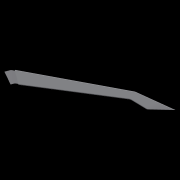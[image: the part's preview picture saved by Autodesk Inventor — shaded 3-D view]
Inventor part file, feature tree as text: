
AUTODESK INVENTOR PART (.ipt)
format: ipt  version: 2020 (Build 240168000, 168)  size: 9,528,320 bytes
history: native  units: in
note: dims shown in document units (in); Inventor stores cm internally (conversion verified against a paired STEP export)
features: other x166, extrude x71, fillet x44, projected_geometry x9, sketch x6, hole x4, loft x3, reference x2, plane x1, move_body x1
ambient origin geometry x8: Origin, YZ Plane, XZ Plane, XY Plane, X Axis, Y Axis, Z Axis, Center Point
bodies: Body (feature_tree), BodyFeature (feature_tree), BodyCut (feature_tree), BodyCutFeature (feature_tree), BodyCutFilletFeature (feature_tree), BodyCutCombineFeature (feature_tree), BodyCutEdgeFilletFeature (feature_tree), BodyRibFrontFilletsFeature (feature_tree), BodyBackRibFilletsFeature (feature_tree), BodyFretboardFilletsFeature (feature_tree), BodyFrontTopFilletsFeature (feature_tree), BodyFrontBottomFilletsFeature (feature_tree), BodyFrontNeckFilletsFeature (feature_tree), Solid22 (feature_tree), Solid23 (feature_tree), Solid62 (feature_tree), Solid64 (feature_tree), Solid65 (feature_tree), Solid68 (feature_tree), Solid50 (feature_tree), Solid52 (feature_tree), Solid54 (feature_tree), Solid56 (feature_tree), Solid57 (feature_tree), Solid59 (feature_tree)
feature tree (307):
  other  "MainBody"
  extrude  "NeckMountsProfileFeature"  Depth=0.5in TaperAngle=0.0deg
  other  "NeckPlane"
  extrude  "8StringFeature"  Depth=4.5in
  extrude  "6StringFeature"  Depth=1.12in
  extrude  "HornFeature"  Depth=0.6788in
  other  "6StringNeckFeature"
  other  "8StringNeckFeature"
  fillet  "InsideCornerFilletsFeature1/8"  Radius=0.6788in
  fillet  "OutsideFilletsFeature1/2"  Radius=0.125in
  fillet  "NeckMountOutsideFilletsFeature1/4"  Radius=0.5in
  fillet  "TipFilletsFeature1/8"  Radius=0.125in
  fillet  "BottomHornTipFilletFeature1/10"  Radius=0.1in
  fillet  "BottomHornFilletsFeature1/8"  Radius=0.125in
  fillet  "InsideHandleFilletsFeature1/2"  Radius=0.5in
  fillet  "InsideHandleFilletsFeature1/8"  Radius=0.125in
  fillet  "InsideTopHornFilletsFeature1/4"  Radius=0.25in
  fillet  "InsideTopHornFilletsFeature1/2"  Radius=0.5in
  fillet  "InsideBottomHornFilletsFeature1/4"  Radius=0.25in
  other  "PickupsOriginal"
  other  "MiddlePlane"
  other  "PickupsCustom"
  other  "PickupsModified"
  extrude  "TopPickupsIndentFeature"  Depth=0.0515in
  extrude  "BottomPickupsIndentFeature"  Depth=0.05in
  extrude  "TopPickupHolesFeature"  Depth=0.05in
  extrude  "BottomPickupHolesFeature"  Depth=0.05in
  fillet  "PickupIndentFilletsFeature"  Radius=5.7in
  other  "Frets"
  other  "FretsPreview"
  other  "TopHornHandleIndent"
  extrude  "TopHornBodyHandleFeature"  Depth=0.05in
  extrude  "TopHornHornHandleFeature"  Depth=0.05in
  other  "HornSculptFeature"
  other  "TopHornHandleFront"
  extrude  "TopHornHandleFrontFeature"  Depth=0.05in
  extrude  "TopHornHandleFront2Feature"  TaperAngle=45.0deg  [1 undecoded]
  extrude  "TopHornHandleFront3Feature"  TaperAngle=120.0deg  [1 undecoded]
  other  "TopHornHandleBack"
  extrude  "TopHornHandleBackFeature"  Depth=0.05in
  extrude  "TopHornHandleBack2Feature"  Depth=0.05in
  extrude  "TopHandleFeature"  Depth=0.05in
  extrude  "TopHandleFrontFeature"  Depth=0.05in
  extrude  "TopHandleBackFeature"  Depth=0.05in
  other  "Tuners"
  hole  "TunerHolesFeature"  [1 undecoded]
  other  "LogoMount"
  extrude  "LogoMountFeature"  Depth=0.05in
  other  "SideProfile"
  extrude  "SideProfileFeature"  Depth=0.05in
  other  "KeyboardCompartmentSidePlane"
  extrude  "KeyboardCompartmentFeature"  Depth=0.05in
  fillet  "KeyboardCompartmentFilletsFeature"  Radius=1.7in
  other  "ControlsBottom"
  other  "ControlsTop2"
  other  "ControlsTop1"
  extrude  "ControlsTop1Feature"  Depth=0.05in
  extrude  "ControlsTop2Feature"  Depth=0.05in
  extrude  "ControlsBottomFeature"  Depth=0.05in
  other  "HornSculptSideProfileFeature"
  fillet  "HornFretboardFilletFeature"  Radius=1.1in
  other  "ElectronicsCompartments"
  other  "InsideFacePlane1"
  other  "InsideFacePlane2"
  other  "InsideFacePlane3"
  extrude  "ElectronicCompartmentTopFeature"  Depth=0.05in
  extrude  "ElectronicCompartmentBottomFeature"  Depth=0.05in
  other  "ElectronicCompartmentsSculpt1Feature"
  other  "ElectronicCompartmentsSculpt2Feature"
  other  "ElectronicCompartmentsSculpt3Feature"
  other  "ElectronicCompartmentsSubtractFeature"
  extrude  "ElectronicCompartmentsSubtract2Feature"  Depth=0.05in
  fillet  "ElectronicCompartmentFillets1Feature"  Radius=1.277in
  fillet  "ElectronicCompartmentFillets2Feature"  Radius=1.277in
  extrude  "ControlIndentsBottomFeature"  Depth=0.05in
  fillet  "ElectronicCompartmentFillets3Feature"  Radius=1.0857in
  fillet  "ElectronicCompartmentFillets4Feature"  Radius=3.0in
  extrude  "ControlIndentsTopFeature"  Depth=0.05in
  other  "ControlIndents2Top"
  extrude  "ControlIndents2TopFeature"  Depth=0.05in
  fillet  "ControlIndents3FilletsFeature"  Radius=3.3665in
  extrude  "ControlIndents2RecutFeature"  Depth=0.05in
  fillet  "ElectronicCompartmentInsideFilletsFeature"  Radius=2.6in
  other  "BottomBridgePickupWirePlane"
  extrude  "BottomBridgePickupWireHoleFeature"  Depth=0.05in
  other  "BottomNeckPickupWirePlane"
  extrude  "BottomNeckPickupWireFeature"  Depth=0.05in
  extrude  "TopPickupWireFeature"  Depth=0.05in
  other  "SeaboardBlockCircuitboardMounts"
  extrude  "SeaboardBlockMountStemFeature"  Depth=0.05in
  extrude  "SeaboardBlockMountsFeature"  Depth=0.05in
  other  "SeaboardBlockKeyMounts"
  extrude  "SeaboardBlockKeyMountsFeature"  Depth=0.05in
  extrude  "SeaboardBlockRibbonsFeature"  Depth=0.05in
  extrude  "TunersTopFeature"  Depth=0.05in
  extrude  "TunersMiddleFeature"  Depth=0.05in
  extrude  "TunersBottomFeature"  Depth=0.05in
  fillet  "TunerFilletsFeature"  Radius=0.45in
  extrude  "NeckCutFeature"  Depth=0.05in
  fillet  "NeckCutFilletFeature"  Radius=1.481in
  other  "NeckCutCombineFeature"
  fillet  "NeckCutEdgeFilletFeature"  Radius=0.25in
  fillet  "NeckCutCornerFilletsFeature"  Radius=0.25in
  extrude  "NeckMountsFeature"  Depth=0.05in
  extrude  "FretMarkersTopFeature"  Depth=0.05in
  extrude  "FretMarkersBottomFeature"  TaperAngle=0.0deg  [1 undecoded]
  extrude  "FretsPreviewFeature"  Depth=0.3937in
  extrude  "FretLocksPreviewFeature"  Depth=0.05in
  hole  "FretLocksHolesFeature"  [1 undecoded]
  extrude  "TopHornHandleBodyFeature"  Depth=0.05in
  other  "TopHornSculpt3Feature"
  other  "TopHornSculpt4Feature"
  other  "TopHornSculpt5Feature"
  fillet  "TopHornHandleBodyFilletsFeature"  [1 undecoded]
  fillet  "TopHornHandleFilletsFeature"  [1 undecoded]
  other  "TopHornAdjustFeature"
  fillet  "TopHornAdjustFilletFeature"  Radius=26.75in
  other  "HandlePlane1"
  other  "HandlePlane2"
  other  "Handle"
  extrude  "HandleBackFeature"  Depth=0.05in
  extrude  "HandleFrontFeature"  Depth=0.05in
  other  "HandleSculpt1Feature"
  other  "HandleSculpt2Feature"
  other  "HandleSculpt3Feature"
  other  "HandleSculpt4Feature"
  other  "HandleSculpt5Feature"
  other  "HandleSculpt6Feature"
  other  "HandleEdit1Feature"
  other  "HandleEdit2Feature"
  fillet  "HandleBodyFilletsFeature"  Radius=0.3333in
  fillet  "HandleRibFilletsFeature"  Radius=0.333in
  other  "HornBackSculptFeature"
  other  "HornHandleBackSculpt1Feature"
  other  "HornHandleBackSculpt2Feature"
  fillet  "HornHandleackSculptFilletsFeature"  Radius=0.1in
  fillet  "HandleMeshFilletsFeature"  Radius=0.1in
  fillet  "HornMeshFillets1Feature"  [1 undecoded]
  fillet  "FretboardEndFilletsFeature"  Radius=0.1in
  other  "KeyboardCompartmentSideProfile"
  extrude  "KeyboardCompartmentExactFeature"  Depth=0.05in
  extrude  "KeyboardCompartmentSideFeature"  Depth=0.05in
  other  "KeyboardCompartmentExactSubtractFeature"
  other  "8NeckSplitFeature"
  other  "8NeckLoftStartPlane"
  other  "8NeckLoftEndPlane"
  loft  "8NeckLoftFeature"
  other  "6NeckSplitForLoftFeature"
  other  "6NeckLoftEndPlane"
  other  "6NeckLoftStartPlane"
  extrude  "OscScreenFeature"  Depth=0.05in
  other  "OscCompartmentPlane"
  other  "OscIndentPlane"
  extrude  "OscCompartmentFeature"  Depth=0.05in
  other  "OscCompartmentSubtractFeature"
  extrude  "OscMountFeature"  Depth=0.05in
  other  "OscCoverIndentPlane"
  extrude  "OscCoverIndentFeature"  TaperAngle=0.0deg  [1 undecoded]
  fillet  "OscCoverIndentFilletsFeature"  Radius=0.25in
  extrude  "OscCoverMountHolesFeature"  Depth=0.05in TaperAngle=0.0deg
  fillet  "ElectronicCompartmentLastFilletFeature"  Radius=0.2in
  loft  "6NeckLoftFeature"
  extrude  "6CloseCutFeature"  Depth=0.05in
  other  "HeadSculpt1Feature"
  other  "HeadThickness"
  other  "HeadSculpt2Feature"
  other  "HeadSculpt3Plane"
  extrude  "HeadSculpt3Feature"  Depth=0.05in
  other  "HeadSculpt4Feature"
  other  "8HeadCombineFeature"
  other  "8HeadCleanupFeature"
  fillet  "8HeadFilletFeature"  Radius=0.5333in
  other  "HeadSculpt5Plane"
  other  "HeadSculpt5Feature"
  other  "HeadSculpt6Feature"
  other  "HeadSculpt7Plane"
  extrude  "HeadSculpt7Feature"  Depth=0.05in
  other  "6StringCombineFeature"
  other  "6NeckFilletSplitFeature"
  other  "8NeckFilletSplitFeature"
  fillet  "InsideHeadFilletFeature"  Radius=0.5in
  other  "CombineFilletsFeature"
  fillet  "HornHeadFilletsFeature"  Radius=5.55in
  fillet  "HornFillet3Feature"  Radius=1.75in
  other  "HornFinalSplitFeature"
  other  "6FinalSplitFeature"
  other  "6CombineFeature"
  other  "8NeckJoin"
  other  "6NeckJoin"
  extrude  "8NeckJoinFeature"  Depth=0.05in
  fillet  "8NeckJoinFilletFeature"  Radius=0.1in
  extrude  "6NeckJoinFeature"  TaperAngle=0.0deg  [1 undecoded]
  extrude  "SeaboardBlockMountHolesFeature"  Depth=0.05in
  extrude  "PickupRecutFeature"  Depth=0.3937in
  extrude  "BackCoverIndentFeature"  Depth=0.05in
  extrude  "ElectronicsCompartmentSupportFeature"  Depth=0.05in
  fillet  "ElectronicsCompartmentSupportFilletsFeature"  Radius=0.2in
  hole  "BackCoverMountsFeature"  [1 undecoded]
  other  "OscCoverBottom"
  other  "OscCoverTopPlane"
  other  "OscCoverMounts"
  loft  "OscCoverFeature"
  extrude  "OscCoverBodyCutFeature"  Depth=0.05in TaperAngle=0.0deg
  fillet  "OscCoverBodyCutFilletsFeature"  Radius=0.125in
  other  "OscCoverBodyCutSubtractFeature"
  fillet  "OscCoverBodyFilletFeature"  Radius=0.1in
  extrude  "OscCoverMountsFeature"  Depth=0.05in
  extrude  "LogoCompartmentFeature"  Depth=0.05in
  other  "LogoMounts"
  extrude  "LogoMountsFeature"  Depth=0.05in
  fillet  "LogoMountsFilletsFeature"  Radius=0.25in
  hole  "LogoMountHolesFeature"  [1 undecoded]
  extrude  "Extrusion179"  Depth=0.05in
  other  "KeyboardCompartment"
  other  "TopHandle"
  other  "TunerLocksBody"
  other  "FretsBody"
  other  "TunersTop"
  other  "TunersMiddle"
  other  "TunersBottom"
  other  "ElectronicCompartments1Body"
  other  "NeckCut"
  other  "NeckMounts"
  other  "TopHornHandle"
  other  "TopHornHandleBody"
  projected_geometry  "Projected Loop22"
  projected_geometry  "Projected Loop23"
  other  "TopHandleFront"
  projected_geometry  "Projected Loop24"
  other  "TopHandleBack"
  other  "HandleBody"
  other  "TopHornSculpt3Plane"
  other  "TopHornSculpt4Plane"
  other  "TopHornSculpt5Plane"
  other  "HandleSculpt1Plane"
  other  "HandleSculpt2Plane"
  other  "HandleSculpt3Plane"
  other  "HandleSculpt4Plane"
  other  "HandleSculpt5Plane"
  other  "HandleSculpt6Plane"
  other  "HornBody"
  other  "8StringBody"
  other  "6StringBody"
  other  "NeckMountsProfile"
  other  "HornBackSculptPlane"
  other  "HornSculptFrontPlane"
  plane  "Work Plane62"
  other  "8NeckStartProfile"
  other  "8NeckEndProfile"
  sketch  "Sketch127"  dims[d8=0.7696in d18=0.5in d119=1.75in d120=0.0in]
  other  "6NeckLoftStartProfile"
  other  "6NeckLoftEndProfile"
  projected_geometry  "Projected Loop27"
  other  "6CloseCut"
  sketch  "Sketch131"  dims[d433=1.0857in d464=4.5in d466=0.25in]
  other  "HeadSculpt1Plane"
  other  "HeadSculpt2Plane"
  other  "HeadSculpt3Profile"
  other  "HeadSculpt4Plane"
  other  "HeadSculpt7Profile"
  other  "6NeckFilletSplit"
  other  "8NeckFilletSplit"
  sketch  "Sketch138"  dims[d501=0.25in d582=1.12in]
  sketch  "Sketch139"  dims[d644=25.0in d654=0.6788in d681=0.6788in d700=0.125in d702=0.5in d703=0.125in d705=0.1in d706=0.125in d707=0.5in d708=0.125in d709=0.25in d710=0.5in d711=0.25in]
  other  "ControlIndentsBottom"
  other  "BottomBridgePickupWireHole"
  other  "BottomNeckPickupWire"
  other  "TopPickupWire"
  other  "HornHandleBackSculpt1Plane"
  other  "HornHandleBackSculpt2Plane"
  sketch  "Sketch165"  dims[d716=2.2835in d717=0.0515in]
  other  "OscScreen"
  other  "OscCompartment"
  other  "OscMount"
  other  "OscCoverPlane"
  other  "OscCoverIndent"
  other  "OscCoverMountHoles"
  projected_geometry  "Projected Loop32"
  other  "KeyboardCompartmentExact"
  projected_geometry  "Projected Loop35"
  other  "SeaboardBlockMountHoles"
  reference  "Reference6"
  reference  "Reference7"
  other  "PickupRecut"
  other  "BackCoverIndent"
  other  "ElectronicsCompartmentSupport"
  other  "BackCoverMounts"
  other  "OscCoverTop"
  other  "OscCoverBody"
  other  "LogoCompartment"
  sketch  "Sketch206"  dims[d718=13.825in d719=0.213in d721=0.9414in d722=1.1649in d724=5.7in d725=7.5379in d726=0.2542in d727=2.0in d728=45.0deg d729=120.0deg d730=0.3642in d731=0.9371in d745=5.6289in d747=6.0in d748=4.3in d750=0.8658in d751=0.6506in d753=0.4054in d754=0.8in d779=0.101in d781=1.7in d782=7.125in d783=2.6in d784=0.933in d787=1.1in d792=3.625in d793=4.0in d819=3.5in d825=1.277in d834=1.277in d836=1.5in d837=1.0857in d838=3.0in d839=2.0in d841=4.5in d846=3.3665in d850=0.1512in d853=2.6in d864=1.5757in d961=0.5in d962=0.5in d963=0.3779in d964=0.3779in d965=0.45in d966=0.45in d967=0.8795in d968=1.1386in d969=1.1386in d970=0.45in d971=4.009in d972=1.481in d979=0.25in d980=0.25in d982=0.1718in d983=0.1718in d984=0.0in d985=0.7874in d987=4.0in d988=0.3937in d990=1.0in d994=2.746in d995=1.481in d996=0.9256in d999=0.0in d1000=0.0in d1022=26.75in d1023=28.0in d1024=25.5in d1026=0.3333in d1041=0.333in d1042=0.1in d1044=0.1in d1048=0.0in d1049=0.0in d1054=0.1in d1055=0.1in d1057=0.748in d1060=0.0in d1061=0.0in d1064=0.4662in d1092=0.7in d1095=1.7in d1100=0.0in d1101=0.0in d1117=0.25in d1118=0.0in d1119=0.3in d1120=0.0in d1122=0.2in d1123=0.0in d1277=0.6459in d1329=0.5333in d1334=0.333in d1335=0.5333in d1339=0.125in d1348=0.5in d1358=5.55in d1359=1.75in d1373=0.2in d1375=0.1in d1376=0.0in d1406=1.125in d1430=3.1496in d1432=0.525in d1433=0.3937in d1435=1.0in d1439=1.8in d1440=1.125in d1441=0.2in d1475=0.1in d1476=0.75in d1477=0.375in d1478=0.25in d1479=0.5635in d1480=0.5in d1481=0.8108in d1483=0.05in d1484=0.0in d1485=0.05in d1486=0.0in d1487=0.05in d1488=0.0in d1489=0.125in d1490=0.1in d1491=2.846in d1492=1.481in d1493=0.5in d1494=0.25in d1496=0.1in d1504=0.13in d1508=0.1in d1511=3.063in d1512=0.1295in d1513=0.1295in d1526=0.5708in d1527=0.1286in d1528=1.3799in d1529=1.3958in d1530=1.1055in d1531=0.8208in d1534=2.3622in d1536=0.45in d1537=0.3937in d1539=1.0in d1574=1.0in d1575=0.0in d1576=0.0in d1577=0.4789in d1578=0.4308in d1579=1.1471in d1580=2.5in d1581=1.275in d1582=1.1845in d1583=1.481in d1584=1.1384in d1585=0.7644in d1586=2.746in d1587=0.264in d1588=0.4in d1589=0.0in d1590=0.75in d1591=0.0in d1592=1.0in d1593=0.0in d1594=1.0in d1595=0.0in d1596=0.144in d1597=3.75in d1598=0.1295in d1599=0.1295in d1638=10.0in d1639=14.2465in d1641=11.25in d1648=0.5in d1649=0.0in d1650=28.0in d1657=1.0in d1659=5.5in d1660=4.25in d1662=0.3333in d1663=0.0in d1664=10.0in d1665=1.0in d1671=0.1in d1672=0.5in d1676=3.0in d1677=2.425in d1682=0.75in d1683=0.0in d1690=1.1878in d1691=0.9817in d1692=1.0844in d1693=0.8784in d1695=0.2in d1696=0.0in d1750=1.525in d1751=0.0in d1752=0.5in d1777=0.5in d1778=0.0in d1779=0.5in d1780=0.0in d1781=0.5in d1782=0.0in d1783=0.6in d1784=0.0in d1790=0.65in d1791=0.0in d1792=0.65in d1793=0.0in d1795=0.125in d1821=0.1in d1828=0.0in d1829=0.0in d1830=0.475in d1831=0.125in d1832=0.125in d1843=3.0403in d1844=2.1333in d1845=0.758in d1847=1.75in d1848=0.0in d1849=1.9in d1850=0.0in d1851=1.9in d1852=0.0in d1858=0.9in d1859=0.0in d1862=0.0in d1863=0.0in d1864=0.5in d1865=0.0in d1866=0.5in d1867=0.0in d1870=0.2056in d1871=0.257in d1872=0.0674in d1875=0.25in d1876=0.0in d1877=0.15in d1880=0.15in d1882=0.05in d1883=0.05in d1885=1.3537in d1887=10.0in d1888=0.1in d1889=0.1in d1890=20.0in d1891=20.0in d1894=0.0618in d1900=0.1in d1901=0.4524in d1903=0.006in d1904=0.0in d1915=0.22in d1921=0.0in d1922=90.0deg d1923=0.0in d1924=90.0deg d1925=1.2in d1926=0.7in d1927=0.3333in d1928=0.001in d1929=0.25in d1930=1.25in d1931=0.25in d1935=0.8in d1936=0.3489in d1937=0.22in d1938=0.25in d1939=0.5in d1940=0.6in d1941=0.15in d1942=0.4in d1943=0.0in d1944=90.0deg d1945=0.0in d1946=90.0deg d1948=1.3333in d1949=2.125in d1951=1.125in d1952=2.55in d1957=3.0in d1958=0.1in d1959=0.1in d1960=0.1in d1961=1.0in d1962=0.0in d1966=1.0in d1967=0.0in d1968=0.44in d1969=0.0in d1975=0.1in d1976=0.1in d1980=10.6875in d1981=5.1875in d1982=0.85in d1983=0.3333in d1985=7.5816in d1987=0.1in d1988=0.0in d1989=0.1875in d1990=0.5333in d1992=150.0deg d1993=3.25in d1996=-0.325in d1997=-0.125in d1998=1.0in d1999=0.0in d2004=0.5in d2005=0.0in d2007=0.0938in d2008=0.5in d2009=0.25in d2010=2.3125in d2011=0.7188in d2015=0.25in d2016=5.0in d2019=0.125in d2020=0.25in d2027=0.2in d2028=0.0in d2029=0.02in d2030=0.0in d2039=0.55in d2047=0.25in d2048=0.25in d2049=0.0in d2050=0.0in d2052=2.295in d2053=0.0in d2056=0.25in d2058=0.25in d2059=0.3333in d2060=0.3333in d2061=0.25in d2062=0.3333in d2063=0.3333in d2064=0.0in d2065=0.0in d2066=0.339in d2067=0.1643in d2068=0.1in d2069=0.1in d2070=0.1in d2071=0.1in d2072=0.1643in d2073=0.1643in d2074=0.1643in d2077=3.3125in d2078=3.313in d2079=0.305in d2080=0.3333in d2081=1.0in d2082=0.0in d2083=0.3333in d2084=0.0in d2086=0.719in d2087=2.3125in d2088=0.125in d2089=0.1in d2090=0.438in d2091=0.438in d2092=0.438in d2093=0.438in d2094=0.25in d2095=0.0in d2096=0.25in d2097=0.25in d2098=2.0in d2100=2.5in d2102=0.75in d2103=0.25in d2104=0.25in d2105=0.0in d2106=0.625in d2111=10.0in d2112=0.125in d2113=0.3333in d2117=1.75in d2118=1.25in d2119=1.625in d2120=0.25in d2121=1.0in d2122=0.1in d2125=0.7in d2132=1.625in d2133=1.0in d2134=0.1in d2135=1.0in d2136=1.0in d2137=0.1in d2138=1.025in d2139=1.025in d2140=0.5in d2141=0.7in d2142=1.075in d2143=0.7in d2144=0.5in d2146=0.25in d2147=0.25in d2148=0.5in d2149=1.75in d2150=0.0in d2151=0.0in d2152=0.035in d2153=0.0in d2154=0.0in d2155=0.0in d2156=-0.325in d2157=1.0in d2158=0.2in d2159=0.0in d2160=1.0in d2161=0.2in d2162=0.0in d2164=1.0in d2165=2.2612in d2166=0.605in d2167=0.01in d2168=0.3333in d2169=0.5388in d2170=0.4in d2171=2.625in d2172=1.375in d2173=0.172in d2174=0.281in d2175=0.5in d2176=0.0in d2177=-2.0in d2178=1.797in d2179=0.0in d2180=-0.125in d2181=0.06in d2182=0.06in d2183=0.505in d2184=0.9375in d2185=2.625in d2186=1.375in d2187=2.5in d2188=1.0313in d2189=0.05in d2190=0.1719in d2191=0.0625in d2192=0.0625in d2193=0.1094in d2194=0.0312in d2195=0.0312in d2196=0.0312in d2197=0.0312in d2198=0.0312in d2199=0.0312in d2200=0.0312in d2201=0.0312in d2202=0.203in d2203=0.0in d2207=-0.2in d2211=0.15in d2212=1.0in d2213=0.0in d2214=0.15in d2215=0.15in d2216=0.1in d2220=0.05in d2221=1.5in d2222=0.0in d2230=0.6836in d2238=1.0in d2239=0.25in d2240=0.1in d2241=0.0689in d2243=1.1408in d2244=0.449in d2245=1.6223in d2246=2.1038in d2247=0.449in d2248=0.0463in d2249=0.4549in d2251=0.3908in d2252=0.3908in d2255=0.8in d2257=3.5in d2259=1.1973in d2261=0.625in d2262=0.625in d2263=0.536in d2264=2.7in d2265=0.25in d2266=0.2in d2267=0.0in d2268=0.2in d2269=0.0in d2278=0.4264in d2279=1.0in d2280=0.0in d2281=21.986in d2282=0.0in d2283=0.1in d2284=0.1in d2285=0.5in d2286=0.0in d2287=0.5333in d2288=0.1in d2293=0.85in d2294=1.0in d2295=0.25in d2296=0.749in d2297=0.0in d2298=0.25in d2299=0.1984in d2300=0.1in d2301=0.0in d2302=0.2in d2303=0.0in d2304=0.481in d2305=0.481in d2306=0.5in d2307=0.25in d2308=0.1in d2309=0.75in d2310=0.375in d2311=0.25in d2312=0.5635in d2313=0.5in d2314=0.8108in d2319=0.0in d2320=0.0in d2321=90.0deg d2322=0.0in d2323=90.0deg d2324=0.5in d2325=0.0in d2326=28.0in d2327=1.0in d2328=1.5in d2329=0.0in d2330=0.2in d2331=0.2in d2333=0.22in d2335=0.12in d2336=0.12in d2337=0.1in d2338=0.1in d2339=0.75in d2340=0.375in d2341=0.25in d2342=0.5635in d2343=0.5in d2344=0.8108in d2347=0.25in d2348=0.3in d2349=0.15in d2350=0.15in d2351=0.3in d2352=0.15in d2353=0.3in d2354=0.25in d2355=0.25in d2356=0.25in d2357=0.25in d2358=0.25in d2359=0.1958in d2360=0.1958in d2361=0.1in d2362=0.1in d2363=0.1in d2364=0.1in d2365=0.2in d2366=0.0in d2369=0.3333in d2370=0.0in d2371=0.05in d2372=0.05in d2373=0.75in d2374=0.375in d2375=0.25in d2376=0.5635in d2377=1.0in d2378=0.8108in d2379=1.05in d2380=0.0in d2381=0.7in d2382=0.6in d620=0.5in d621=0.0344in d622=0.5in d623=0.0344in d1625=0.5in d1626=0.0344in d1627=0.5in d1628=0.0344in d1730=0.5in d1731=0.0344in d1732=0.5in d1733=0.0344in d1822=0.5in d1823=0.0344in d1824=0.5in d1825=0.0344in d1837=0.5in d1838=0.0344in d1839=0.5in d1840=0.0344in d1860=0.5in d1861=0.0344in d1947=0.5in d1950=0.0344in d2012=0.5in d2013=0.0344in d2101=0.5in]
  projected_geometry  "Projected Loop40"
  projected_geometry  "Projected Loop41"
  projected_geometry  "Projected Loop42"
  other  "Delete13"
  move_body  "Move3"
  other  "Delete14"
  other  "6StringNeckCombineBody"
  other  "8StringNeckBody"
  other  "6StringNeckBody"
  other  "TopHornBody"
  other  "8StringCombinedBody"
  other  "6StringCombinedBody"
  other  "Delete18"
  other  "<userpath>\Desktop\switchback\src\switchback-exploded.iam"
  other  "switchback-exploded.iam"
  other  "seaboard-block-keyboard:1"
note: 12 required parameter values undecoded (feature->parameter linkage not recoverable at this tier; creation-order binding heuristic only, values carry confidence <= 0.55)
